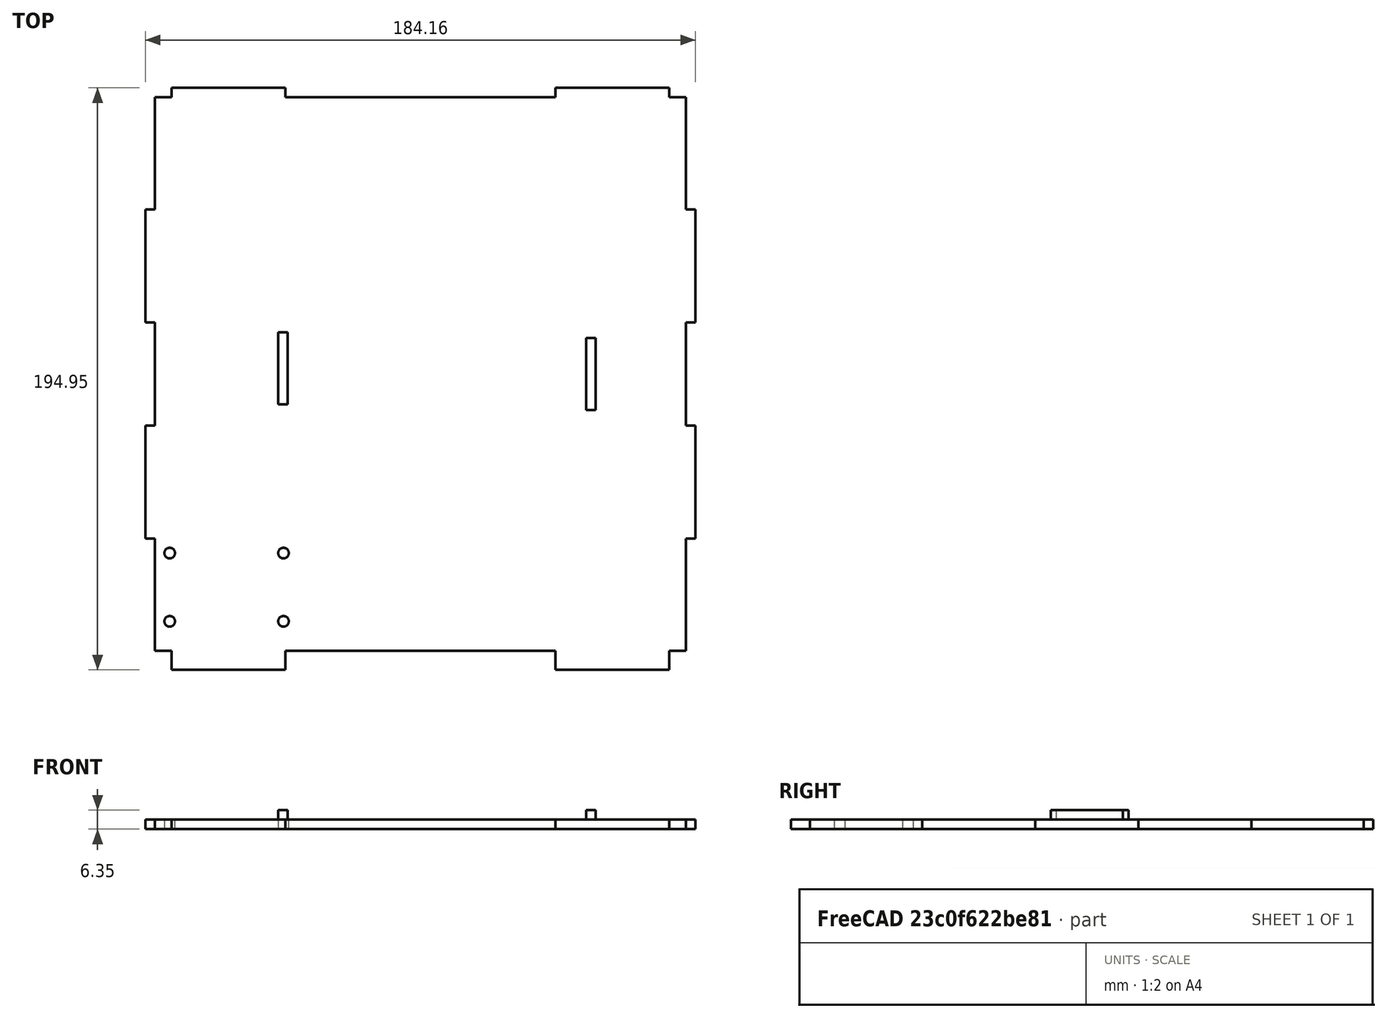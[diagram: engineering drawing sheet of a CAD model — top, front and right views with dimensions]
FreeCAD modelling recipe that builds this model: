
FCSTD DOCUMENT  (FreeCAD 0.18R4 (GitTag))
Label: rpr68k
License: All rights reserved
LicenseURL: http://en.wikipedia.org/wiki/All_rights_reserved
objects: Sketcher::SketchObject×2, PartDesign::Pad×2, PartDesign::Body×1, App::Part×1, Mesh::Feature×1
note: 7 computed .brp shape members not serialized (recipe doc carries the construction recipe); baked Part::Feature solids carry a one-line shape summary decoded from their .brp

FEATURE [Sketcher::SketchObject] Sketch
  MapMode = 5
  Support = -> [XY_Plane001]
  sketch-geometry (40):
    g0: LineSegment StartX=-88.9 StartY=92.71 StartZ=0 EndX=-83.312 EndY=92.71 EndZ=0
    g1: LineSegment StartX=-83.312 StartY=92.71 StartZ=0 EndX=-83.312 EndY=95.885 EndZ=0
    g2: LineSegment StartX=-83.312 StartY=95.885 StartZ=0 EndX=-45.212 EndY=95.885 EndZ=0
    g3: LineSegment StartX=-45.212 StartY=95.885 StartZ=0 EndX=-45.212 EndY=92.71 EndZ=0
    g4: LineSegment StartX=-45.212 StartY=92.71 StartZ=0 EndX=45.212 EndY=92.71 EndZ=0
    g5: LineSegment StartX=45.212 StartY=92.71 StartZ=0 EndX=45.212 EndY=95.885 EndZ=0
    g6: LineSegment StartX=45.212 StartY=95.885 StartZ=0 EndX=83.312 EndY=95.885 EndZ=0
    g7: LineSegment StartX=83.312 StartY=95.885 StartZ=0 EndX=83.312 EndY=92.71 EndZ=0
    g8: LineSegment StartX=83.312 StartY=92.71 StartZ=0 EndX=88.9 EndY=92.71 EndZ=0
    g9: LineSegment StartX=88.9 StartY=92.71 StartZ=0 EndX=88.9 EndY=55.118 EndZ=0
    g10: LineSegment StartX=88.9 StartY=55.118 StartZ=0 EndX=92.075 EndY=55.118 EndZ=0
    g11: LineSegment StartX=92.075 StartY=55.118 StartZ=0 EndX=92.075 EndY=17.272 EndZ=0
    g12: LineSegment StartX=92.075 StartY=17.272 StartZ=0 EndX=88.9 EndY=17.272 EndZ=0
    g13: LineSegment StartX=88.9 StartY=17.272 StartZ=0 EndX=88.9 EndY=-17.272 EndZ=0
    g14: LineSegment StartX=88.9 StartY=-17.272 StartZ=0 EndX=92.075 EndY=-17.272 EndZ=0
    g15: LineSegment StartX=92.075 StartY=-17.272 StartZ=0 EndX=92.075 EndY=-55.118 EndZ=0
    g16: LineSegment StartX=92.075 StartY=-55.118 StartZ=0 EndX=88.9 EndY=-55.118 EndZ=0
    g17: LineSegment StartX=88.9 StartY=-55.118 StartZ=0 EndX=88.9 EndY=-92.71 EndZ=0
    g18: LineSegment StartX=88.9 StartY=-92.71 StartZ=0 EndX=83.312 EndY=-92.71 EndZ=0
    g19: LineSegment StartX=83.312 StartY=-92.71 StartZ=0 EndX=83.312 EndY=-99.06 EndZ=0
    g20: LineSegment StartX=83.312 StartY=-99.06 StartZ=0 EndX=45.212 EndY=-99.06 EndZ=0
    g21: LineSegment StartX=45.212 StartY=-99.06 StartZ=0 EndX=45.212 EndY=-92.71 EndZ=0
    g22: LineSegment StartX=45.212 StartY=-92.71 StartZ=0 EndX=-45.212 EndY=-92.71 EndZ=0
    g23: LineSegment StartX=-45.212 StartY=-92.71 StartZ=0 EndX=-45.212 EndY=-99.06 EndZ=0
    g24: LineSegment StartX=-45.212 StartY=-99.06 StartZ=0 EndX=-83.312 EndY=-99.06 EndZ=0
    g25: LineSegment StartX=-83.312 StartY=-99.06 StartZ=0 EndX=-83.312 EndY=-92.71 EndZ=0
    g26: LineSegment StartX=-83.312 StartY=-92.71 StartZ=0 EndX=-88.9 EndY=-92.71 EndZ=0
    g27: LineSegment StartX=-88.9 StartY=-92.71 StartZ=0 EndX=-88.9 EndY=-55.118 EndZ=0
    g28: LineSegment StartX=-88.9 StartY=-55.118 StartZ=0 EndX=-92.075 EndY=-55.118 EndZ=0
    g29: LineSegment StartX=-92.075 StartY=-55.118 StartZ=0 EndX=-92.075 EndY=-17.272 EndZ=0
    g30: LineSegment StartX=-92.075 StartY=-17.272 StartZ=0 EndX=-88.9 EndY=-17.272 EndZ=0
    g31: LineSegment StartX=-88.9 StartY=-17.272 StartZ=0 EndX=-88.9 EndY=17.272 EndZ=0
    g32: LineSegment StartX=-88.9 StartY=17.272 StartZ=0 EndX=-92.075 EndY=17.272 EndZ=0
    g33: LineSegment StartX=-92.075 StartY=17.272 StartZ=0 EndX=-92.075 EndY=55.118 EndZ=0
    g34: LineSegment StartX=-92.075 StartY=55.118 StartZ=0 EndX=-88.9 EndY=55.118 EndZ=0
    g35: LineSegment StartX=-88.9 StartY=55.118 StartZ=0 EndX=-88.9 EndY=92.71 EndZ=0
    g36: Circle CenterX=-83.947 CenterY=-82.804 CenterZ=0 NormalX=0 NormalY=0 NormalZ=1 AngleXU=0 Radius=1.778
    g37: Circle CenterX=-83.947 CenterY=-59.944 CenterZ=0 NormalX=0 NormalY=0 NormalZ=1 AngleXU=0 Radius=1.778
    g38: Circle CenterX=-45.847 CenterY=-59.944 CenterZ=0 NormalX=0 NormalY=0 NormalZ=1 AngleXU=0 Radius=1.778
    g39: Circle CenterX=-45.847 CenterY=-82.804 CenterZ=0 NormalX=0 NormalY=0 NormalZ=1 AngleXU=0 Radius=1.778
  constraints (118):
    c: Horizontal(g0)
    c: Coincident(g0,g1)
    c: Vertical(g1)
    c: Coincident(g1,g2)
    c: Horizontal(g2)
    c: Coincident(g2,g3)
    c: Coincident(g3,g4)
    c: Coincident(g4,g5)
    c: Coincident(g5,g6)
    c: Horizontal(g6)
    c: Coincident(g6,g7)
    c: Coincident(g7,g8)
    c: Horizontal(g8)
    c: Coincident(g8,g9)
    c: Coincident(g9,g10)
    c: Coincident(g10,g11)
    c: Coincident(g11,g12)
    c: Coincident(g12,g13)
    c: Coincident(g13,g14)
    c: Coincident(g14,g15)
    c: Coincident(g15,g16)
    c: Coincident(g16,g17)
    c: Vertical(g17)
    c: Coincident(g17,g18)
    c: Coincident(g18,g19)
    c: Vertical(g19)
    c: Coincident(g19,g20)
    c: Horizontal(g20)
    c: Coincident(g20,g21)
    c: Coincident(g21,g22)
    c: Horizontal(g22)
    c: Coincident(g22,g23)
    c: Vertical(g23)
    c: Coincident(g23,g24)
    c: Horizontal(g24)
    c: Coincident(g24,g25)
    c: Vertical(g25)
    c: Coincident(g25,g26)
    c: Coincident(g26,g27)
    c: Vertical(g27)
    c: Coincident(g27,g28)
    c: Coincident(g28,g29)
    c: Coincident(g29,g30)
    c: Coincident(g30,g31)
    c: Coincident(g31,g32)
    c: Coincident(g32,g33)
    c: Coincident(g33,g34)
    c: Coincident(g34,g35)
    c: Coincident(g35,g0)
    c: Vertical(g3)
    c: Vertical(g5)
    c: Vertical(g7)
    c: Vertical(g35)
    c: Vertical(g29)
    c: Vertical(g33)
    c: Vertical(g9)
    c: Vertical(g11)
    c: Vertical(g13)
    c: Vertical(g15)
    c: Horizontal(g34)
    c: Horizontal(g32)
    c: Horizontal(g30)
    c: Horizontal(g28)
    c: Horizontal(g16)
    c: Horizontal(g14)
    c: Horizontal(g12)
    c: Horizontal(g10)
    c: Equal(g31,g13)
    c: Equal(g4,g22)
    c: Equal(g29,g33)
    c: Equal(g33,g11)
    c: Equal(g11,g15)
    c: Equal(g2,g6)
    c: Equal(g6,g20)
    c: Equal(g20,g24)
    c: Horizontal(g26)
    c: Horizontal(g18)
    c: Equal(g0,g8)
    c: Equal(g8,g26)
    c: Equal(g26,g18)
    c: Equal(g1,g3)
    c: Equal(g3,g5)
    c: Equal(g5,g7)
    c: Equal(g25,g23)
    c: Equal(g23,g21)
    c: Equal(g21,g19)
    c: Equal(g34,g32)
    c: Equal(g32,g30)
    c: Equal(g30,g28)
    c: Equal(g28,g10)
    c: Equal(g10,g12)
    c: Equal(g12,g14)
    c: Equal(g14,g16)
    c: Symmetric(g3,g4,g-2)
    c: Symmetric(g31,g30,g-1)
    c: DistanceX(g33,g34) = 3.175
    c: DistanceY(g0,g1) = 3.175
    c: DistanceY(g24,g25) = 6.35
    c: DistanceY(g32,g33) = 37.846
    c: Equal(g35,g9)
    c: Equal(g35,g27)
    c: DistanceX(g1,g2) = 38.1
    c: DistanceX(g3,g4) = 90.424
    c: Equal(g36,g37)
    c: Equal(g37,g38)
    c: Equal(g38,g39)
    c: Diameter(g36) = 3.556
    c: DistanceY(g36,g37) = 22.86
    c: DistanceY(g39,g38) = 22.86
    c: DistanceX(g37,g38) = 38.1
    c: DistanceX(g36,g39) = 38.1
    c: DistanceY(g25,g36) = 9.906
    c: DistanceY(g25,g39) = 9.906
    c: DistanceX(g27,g36) = 4.953
    c: DistanceX(g27,g37) = 4.953
    c: DistanceY(g26,g27) = 37.592
    c: DistanceY(g-1,g0) = 92.71
    c: DistanceX(g31,g-1) = 88.9
FEATURE [Sketcher::SketchObject] Sketch001
  MapMode = 5
  Placement = pos=(0,0,3.175) rot=(0,0,1;0rad)
  sketch-geometry (8):
    g0: LineSegment StartX=55.5625 StartY=12.065 StartZ=0 EndX=58.7375 EndY=12.065 EndZ=0
    g1: LineSegment StartX=58.7375 StartY=12.065 StartZ=0 EndX=58.7375 EndY=-12.065 EndZ=0
    g2: LineSegment StartX=58.7375 StartY=-12.065 StartZ=0 EndX=55.5625 EndY=-12.065 EndZ=0
    g3: LineSegment StartX=55.5625 StartY=-12.065 StartZ=0 EndX=55.5625 EndY=12.065 EndZ=0
    g4: LineSegment StartX=-47.625 StartY=13.97 StartZ=0 EndX=-44.45 EndY=13.97 EndZ=0
    g5: LineSegment StartX=-44.45 StartY=13.97 StartZ=0 EndX=-44.45 EndY=-10.16 EndZ=0
    g6: LineSegment StartX=-44.45 StartY=-10.16 StartZ=0 EndX=-47.625 EndY=-10.16 EndZ=0
    g7: LineSegment StartX=-47.625 StartY=-10.16 StartZ=0 EndX=-47.625 EndY=13.97 EndZ=0
  constraints (23):
    c: Coincident(g0,g1)
    c: Coincident(g1,g2)
    c: Coincident(g2,g3)
    c: Coincident(g3,g0)
    c: Horizontal(g0)
    c: Horizontal(g2)
    c: Vertical(g1)
    c: DistanceX(g0,g0) = 3.175
    c: DistanceY(g2,g0) = 24.13
    c: DistanceX(g-1,g0) = 55.5625
    c: Coincident(g4,g5)
    c: Coincident(g5,g6)
    c: Coincident(g6,g7)
    c: Coincident(g7,g4)
    c: Horizontal(g4)
    c: Horizontal(g6)
    c: Vertical(g7)
    c: DistanceX(g4,g4) = 3.175
    c: DistanceY(g5,g4) = 24.13
    c: DistanceY(g-1,g4) = 13.97
    c: Symmetric(g0,g2,g-1)
    c: DistanceX(g4,g-1) = 44.45
    c: Equal(g4,g6)
FEATURE [PartDesign::Pad] Pad
  Length = 3.175
  Length2 = 99.9998
  Profile = -> Sketch
  Type = 0
FEATURE [PartDesign::Pad] Pad001
  BaseFeature = -> Pad
  Length = 3.175
  Length2 = 99.9998
  Profile = -> Sketch001
  Type = 0
FEATURE [PartDesign::Body] Body
  Group = -> [Sketch,Sketch001,Pad,Pad001]
  Origin = -> Origin001
  Tip = -> Pad001
FEATURE [App::Part] Part
  Group = -> [Body]
  Origin = -> Origin
FEATURE [Mesh::Feature] Mesh  label="rpr68k"
